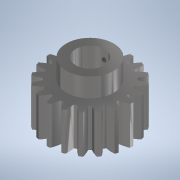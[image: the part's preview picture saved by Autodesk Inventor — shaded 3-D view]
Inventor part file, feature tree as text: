
AUTODESK INVENTOR PART (.ipt)
format: ipt  version: 2021 (Build 250183000, 183)  size: 249,344 bytes
history: native  units: mm (DEFAULTED — no unit token found)
features: sketch x5, plane x4, extrude x3, other x3, hole x1
ambient origin geometry x8: Origin, YZ Plane, XZ Plane, XY Plane, X Axis, Y Axis, Z Axis, Center Point
bodies: Solid1 (feature_tree)
feature tree (16):
  extrude  "Extrusion1"  Depth=20.0mm TaperAngle=0.0deg
  plane  "Work Plane2"
  plane  "Work Plane8"
  plane  "Work Plane9"
  other  "Engranaje recto"
  extrude  "Extrusión2"  Depth=10.0mm TaperAngle=0.0deg
  extrude  "Extrusión3"  Depth=1.570796mm TaperAngle=0.0deg
  plane  "Plano de trabajo11"
  hole  "Agujero1"  [1 undecoded]
  sketch  "Sketch1"  dims[d0=44.0mm d1=20.0mm d2=0.0mm]
  sketch  "Sketch2"  dims[d3=40.0mm d4=10.0mm d5=0.0mm]
  other  "Srf1"
  sketch  "Boceto3"  dims[d16=70.0mm d17=0.0mm d34=1.570796mm]
  sketch  "Boceto4"  dims[d39=0.0mm d41=0.0mm]
  sketch  "Boceto5"  dims[d43=70.0mm d46=70.0mm d47=0.0mm d48=0.0mm d49=25.0mm d51=10.0mm d52=0.0mm d53=15.0mm d54=30.0mm d55=0.0mm d56=5.0mm d57=3.0mm d58=2.487mm d59=6.35mm d60=4.0mm d61=2.0mm d62=90.0deg d63=9.525mm d64=20.594885mm]
  other  "Diámetro de separación"
note: 1 required parameter value undecoded (feature->parameter linkage not recoverable at this tier; creation-order binding heuristic only, values carry confidence <= 0.55)
